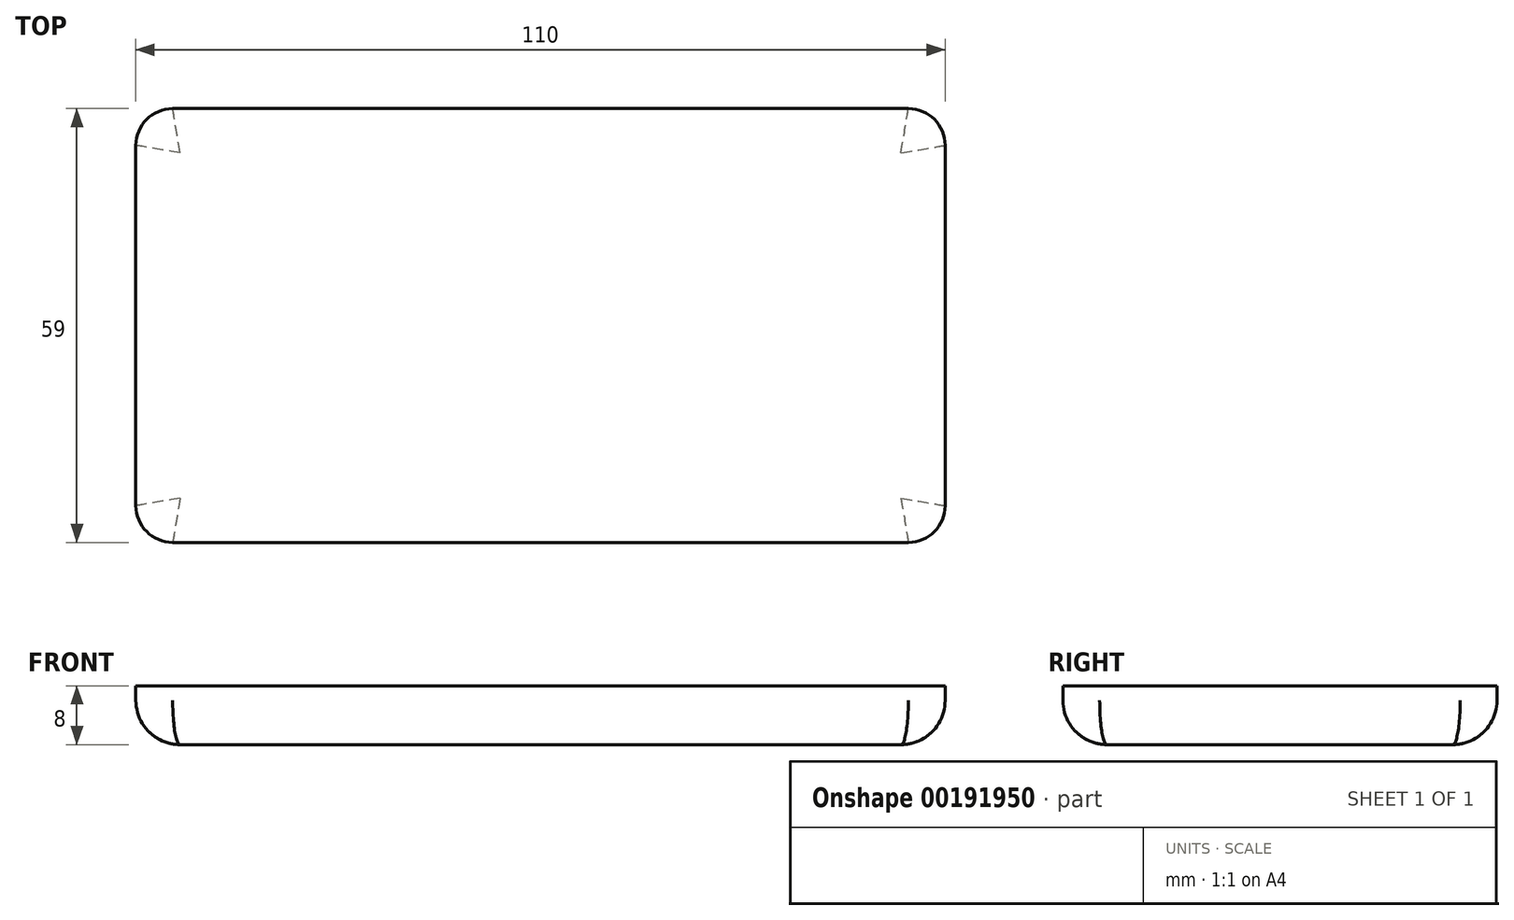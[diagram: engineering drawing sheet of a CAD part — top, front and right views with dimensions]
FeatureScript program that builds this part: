
annotation { "Feature Type Name" : "Feature", "Feature Type Description" : "" }
export const myFeature = defineFeature(function(context is Context, id is Id, definition is map)
    precondition{}
    {
        {
            var Q0;
            Q0=qCreatedBy(makeId("Top.planeOp"),FACE);
            var sketch = newSketch(context, id + "F0", { "sketchPlane" : qUnion([Q0])});
            skLineSegment(sketch, "E0.bottom", {"start": v(-55, 29.5) * mm, "end": v(55, 29.5) * mm});
            skLineSegment(sketch, "E0.top", {"start": v(-55, -29.5) * mm, "end": v(55, -29.5) * mm});
            skLineSegment(sketch, "E0.left", {"start": v(-55, 29.5) * mm, "end": v(-55, -29.5) * mm});
            skLineSegment(sketch, "E0.right", {"start": v(55, 29.5) * mm, "end": v(55, -29.5) * mm});
            skPoint(sketch, "E0.middle", {"position": v(0, 0) * mm});
            skSolve(sketch);
        }
        {
            var Q0;
            Q0=makeQuery(id+"F0.imprint","IMPRINT",FACE,{"disambiguationData":[TD([[makeQuery(id+"F0.imprint","IMPRINT",EDGE,{"derivedFrom":sQuery(id+"F0.wireOp",EDGE,"E0.bottom")}),-1.0]])]});
            extrude(context, id + "F1", {"entities" : qUnion([Q0]), "depth" : 8 * mm});
        }
        {
            var Q0;
            Q0=makeQuery(id+"F1.opExtrude","SWEPT_EDGE",EDGE,{"disambiguationData":[OSD([sQuery(id+"F0.wireOp",EDGE,"E0.top"),sQuery(id+"F0.wireOp",EDGE,"E0.left")])]});
            var Q1;
            Q1=makeQuery(id+"F1.opExtrude","SWEPT_EDGE",EDGE,{"disambiguationData":[OSD([sQuery(id+"F0.wireOp",EDGE,"E0.top"),sQuery(id+"F0.wireOp",EDGE,"E0.right")])]});
            var Q2;
            Q2=makeQuery(id+"F1.opExtrude","SWEPT_EDGE",EDGE,{"disambiguationData":[OSD([sQuery(id+"F0.wireOp",EDGE,"E0.bottom"),sQuery(id+"F0.wireOp",EDGE,"E0.right")])]});
            var Q3;
            Q3=makeQuery(id+"F1.opExtrude","SWEPT_EDGE",EDGE,{"disambiguationData":[OSD([sQuery(id+"F0.wireOp",EDGE,"E0.bottom"),sQuery(id+"F0.wireOp",EDGE,"E0.left")])]});
            fillet(context, id + "F2", {"entities" : qUnion([Q0, Q1, Q2, Q3]), "radius" : 5 * mm, "tangentPropagation" : true, "allowEdgeOverflow" : false});
        }
        {
            var Q0;
            Q0=makeQuery(id+"F1.opExtrude","CAP_FACE",FACE,{"disambiguationData":[OSD([sQuery(id+"F0.wireOp",EDGE,"E0.bottom"),sQuery(id+"F0.wireOp",EDGE,"E0.top"),sQuery(id+"F0.wireOp",EDGE,"E0.left"),sQuery(id+"F0.wireOp",EDGE,"E0.right")])],"isStart":true});
            fillet(context, id + "F3", {"entities" : qUnion([Q0]), "radius" : 6 * mm, "tangentPropagation" : true, "allowEdgeOverflow" : false});
        }
    });
